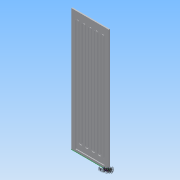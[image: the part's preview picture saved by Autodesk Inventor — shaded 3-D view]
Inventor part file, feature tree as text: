
AUTODESK INVENTOR PART (.ipt)
format: ipt  version: 2013 (Build 170138000, 138)  size: 210,432 bytes
history: native  units: in
note: dims shown in document units (in); Inventor stores cm internally (conversion verified against a paired STEP export)
features: other x7, extrude x2, sketch x1
ambient origin geometry x8: Origin, YZ Plane, XZ Plane, XY Plane, X Axis, Y Axis, Z Axis, Center Point
bodies: Solid1 (feature_tree)
feature tree (10):
  other  "Blocks"
  extrude  "Extrusion1"  Depth=78.0in
  extrude  "Extrusion3"  TaperAngle=0.0deg  [1 undecoded]
  sketch  "Sketch1"  dims[d1=23.8125in d2=78.0in d3=0.0in d4=66.0in d6=1.0in d7=2.9in d9=0.24in d10=0.24in d18=1.5in d19=78.0in d20=78.0in d21=22.3125in d22=66.0in d23=2.0in d25=0.24in d26=0.24in d29=2.0in d31=1.5in d32=3.3in d33=1.74in d34=1.0in d35=0.1875in d37=5.46in d38=6.54in d41=66.0in d42=2.0in d43=0.24in d44=0.24in d45=2.0in d46=66.0in d47=2.0in d48=0.48in d49=66.0in d50=2.0in d51=1.0in d52=0.24in d53=0.24in d54=66.0in d55=0.48in d63=0.5in d64=0.0in d73=0.55in d74=0.47in d75=0.5in d76=0.58in d79=1.5in d80=0.48in d81=0.5in d83=0.5118in d84=0.375in d85=0.205in d86=0.6056in d87=1.1056in d88=0.25in]
  other  "LEDPocket"
  other  "TwoLineColumn"
  other  "TwoLineColumnEnd"
  other  "15mm Neon profile"
  other  "15mm Neon profile:1"
  other  "15mm Neon profile:2"
note: 1 required parameter value undecoded (feature->parameter linkage not recoverable at this tier; creation-order binding heuristic only, values carry confidence <= 0.55)
